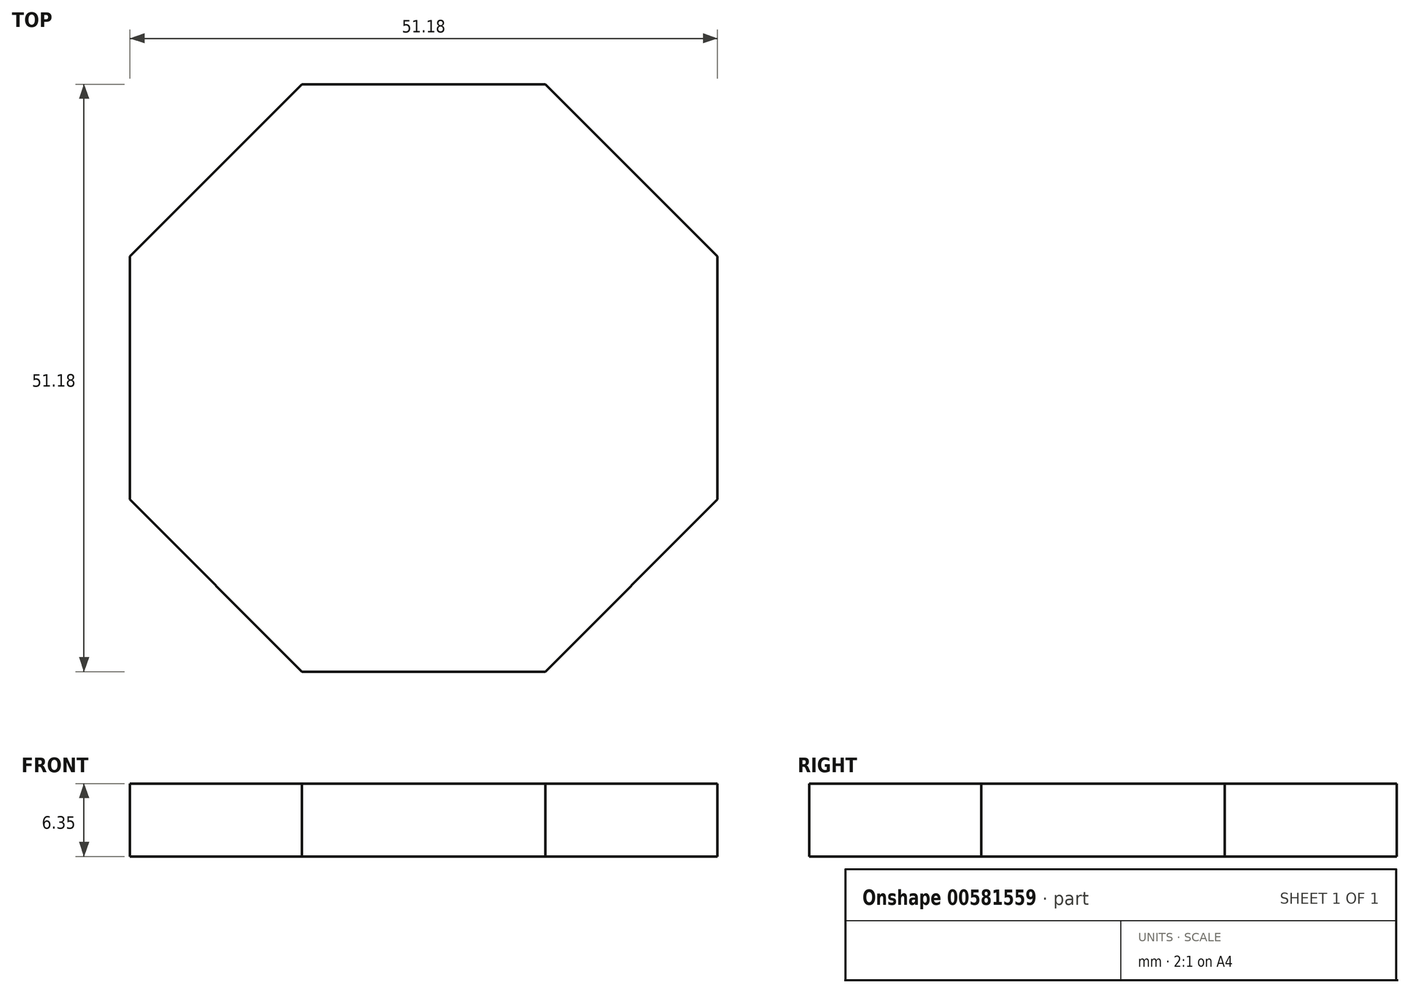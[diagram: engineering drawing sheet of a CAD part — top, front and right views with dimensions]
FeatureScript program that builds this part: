
annotation { "Feature Type Name" : "Feature", "Feature Type Description" : "" }
export const myFeature = defineFeature(function(context is Context, id is Id, definition is map)
    precondition{}
    {
        {
            var Q0;
            Q0=qCreatedBy(makeId("Top.planeOp"),FACE);
            var sketch = newSketch(context, id + "F0", { "sketchPlane" : qUnion([Q0])});
            skLineSegment(sketch, "E0.bottom", {"start": v(-24.81, 35.21) * mm, "end": v(26.37, 35.21) * mm});
            skLineSegment(sketch, "E0.top", {"start": v(-24.81, -15.97) * mm, "end": v(26.37, -15.97) * mm});
            skLineSegment(sketch, "E0.left", {"start": v(-24.81, 35.21) * mm, "end": v(-24.81, -15.97) * mm});
            skLineSegment(sketch, "E0.right", {"start": v(26.37, 35.21) * mm, "end": v(26.37, -15.97) * mm});
            skSolve(sketch);
        }
        {
            var Q0;
            Q0 = qSketchRegion(id + "F0", true);
            extrude(context, id + "F1", {"entities" : qUnion([Q0]), "depth" : 6.35 * mm, "offsetDistance" : 25.4 * mm});
        }
        {
            var Q0;
            Q0=makeQuery(id+"F1.opExtrude","CAP_FACE",FACE,{"disambiguationData":[OSD([sQuery(id+"F0.wireOp",EDGE,"E0.bottom"),sQuery(id+"F0.wireOp",EDGE,"E0.top"),sQuery(id+"F0.wireOp",EDGE,"E0.left"),sQuery(id+"F0.wireOp",EDGE,"E0.right")])],"isStart":false});
            var sketch = newSketch(context, id + "F2", { "sketchPlane" : qUnion([Q0])});
            skLineSegment(sketch, "E1", {"start": v(-24.81, 20.22) * mm, "end": v(-9.82, 35.21) * mm});
            skLineSegment(sketch, "E2", {"start": v(-9.82, 35.21) * mm, "end": v(11.38, 35.21) * mm});
            skLineSegment(sketch, "E3", {"start": v(11.38, 35.21) * mm, "end": v(26.37, 20.22) * mm});
            skLineSegment(sketch, "E4", {"start": v(26.37, -0.98) * mm, "end": v(26.37, 20.22) * mm});
            skLineSegment(sketch, "E5", {"start": v(-24.81, 20.22) * mm, "end": v(-24.81, -0.98) * mm});
            skLineSegment(sketch, "E6", {"start": v(-9.82, -15.97) * mm, "end": v(11.38, -15.97) * mm});
            skLineSegment(sketch, "E7", {"start": v(11.38, -15.97) * mm, "end": v(26.37, -0.98) * mm});
            skLineSegment(sketch, "E8", {"start": v(-9.82, -15.97) * mm, "end": v(-24.81, -0.98) * mm});
            skSolve(sketch);
        }
        {
            var Q0;
            {var subQ0=sQuery(id+"F2.wireOp",EDGE,"E1");Q0=makeQuery(id+"F2.imprint","IMPRINT",FACE,{"disambiguationData":[TD([[makeQuery(id+"F2.imprint","IMPRINT",EDGE,{"derivedFrom":subQ0}),1.0]])]});}
            var Q1;
            {var subQ0=sQuery(id+"F2.wireOp",EDGE,"E3");Q1=makeQuery(id+"F2.imprint","IMPRINT",FACE,{"disambiguationData":[TD([[makeQuery(id+"F2.imprint","IMPRINT",EDGE,{"derivedFrom":subQ0}),1.0]])]});}
            var Q2;
            {var subQ0=sQuery(id+"F2.wireOp",EDGE,"E8");Q2=makeQuery(id+"F2.imprint","IMPRINT",FACE,{"disambiguationData":[TD([[makeQuery(id+"F2.imprint","IMPRINT",EDGE,{"derivedFrom":subQ0}),1.0]])]});}
            var Q3;
            {var subQ0=sQuery(id+"F2.wireOp",EDGE,"E7");Q3=makeQuery(id+"F2.imprint","IMPRINT",FACE,{"disambiguationData":[TD([[makeQuery(id+"F2.imprint","IMPRINT",EDGE,{"derivedFrom":subQ0}),-1.0]])]});}
            extrude(context, id + "F3", {"entities" : qUnion([Q0, Q1, Q2, Q3]), "operationType" : NewBodyOperationType.REMOVE, "oppositeDirection" : true, "depth" : 25.4 * mm, "offsetDistance" : 25.4 * mm});
        }
    });
